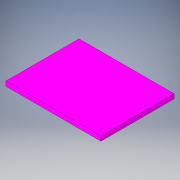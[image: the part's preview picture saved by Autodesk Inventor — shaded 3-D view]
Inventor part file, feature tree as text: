
AUTODESK INVENTOR PART (.ipt)
format: ipt  version: 2019 (Build 230136000, 136)  size: 102,912 bytes
history: native  units: mm
features: extrude x1, sketch x1
ambient origin geometry x8: Origin, YZ Plane, XZ Plane, XY Plane, X Axis, Y Axis, Z Axis, Center Point
bodies: Solid1 (feature_tree)
feature tree (2):
  extrude  "Extrusion1"  Depth=50.0mm
  sketch  "Sketch1"  dims[d0=65.0mm d1=50.0mm d2=3.18mm d3=0.0mm]
